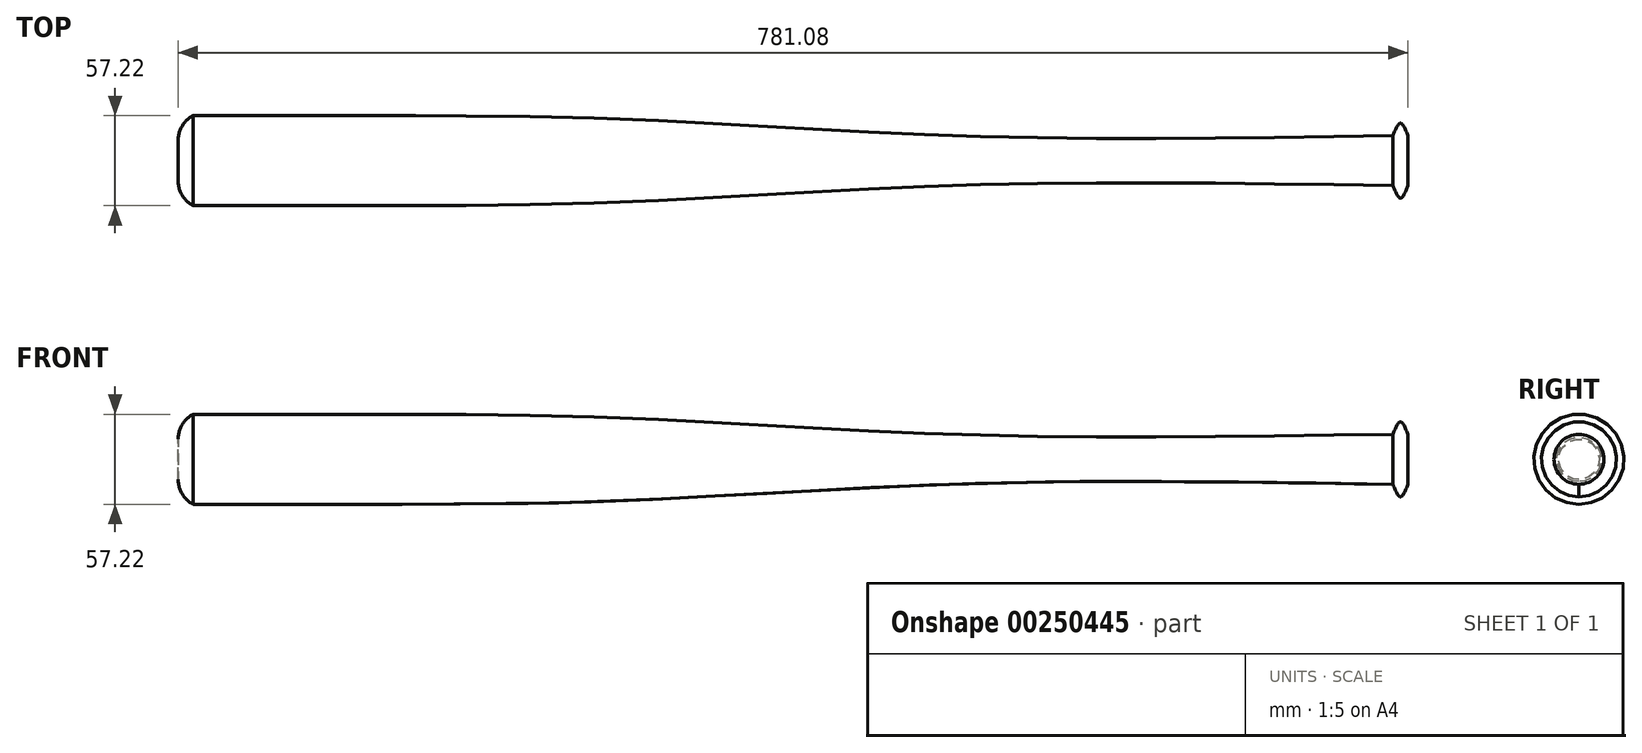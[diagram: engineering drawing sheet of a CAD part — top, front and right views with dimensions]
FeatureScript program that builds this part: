
annotation { "Feature Type Name" : "Feature", "Feature Type Description" : "" }
export const myFeature = defineFeature(function(context is Context, id is Id, definition is map)
    precondition{}
    {
        {
            var Q0;
            Q0=qCreatedBy(makeId("Right.planeOp"),FACE);
            var sketch = newSketch(context, id + "F0", { "sketchPlane" : qUnion([Q0])});
            skCircle(sketch, "E0", {"center": v(0, 0) * mm, "radius": 23.81 * mm});
            skSolve(sketch);
        }
        {
            var Q0;
            Q0=qCreatedBy(makeId("Right.planeOp"),FACE);
            cPlane(context, id + "F1", {"entities" : qUnion([Q0]), "cplaneType" : CPlaneType.OFFSET, "offset" : 4.78 * mm, "oppositeDirection" : true, "width" : 152.4 * mm, "height" : 152.4 * mm});
        }
        {
            var Q0;
            Q0=qCreatedBy(id+"F1.planeOp",FACE);
            var sketch = newSketch(context, id + "F2", { "sketchPlane" : qUnion([Q0])});
            skCircle(sketch, "E1", {"center": v(0, 0) * mm, "radius": 15.88 * mm});
            skSolve(sketch);
        }
        {
            var Q0;
            Q0=qCreatedBy(id+"F1.planeOp",FACE);
            cPlane(context, id + "F3", {"entities" : qUnion([Q0]), "cplaneType" : CPlaneType.OFFSET, "offset" : 127 * mm, "oppositeDirection" : true, "width" : 152.4 * mm, "height" : 152.4 * mm});
        }
        {
            var Q0;
            Q0=qCreatedBy(id+"F3.planeOp",FACE);
            var sketch = newSketch(context, id + "F4", { "sketchPlane" : qUnion([Q0])});
            skCircle(sketch, "E2", {"center": v(0, 0) * mm, "radius": 14.29 * mm});
            skSolve(sketch);
        }
        {
            var Q0;
            Q0=qCreatedBy(makeId("Right.planeOp"),FACE);
            cPlane(context, id + "F5", {"entities" : qUnion([Q0]), "cplaneType" : CPlaneType.OFFSET, "offset" : 4.78 * mm, "width" : 152.4 * mm, "height" : 152.4 * mm});
        }
        {
            var Q0;
            Q0=qCreatedBy(id+"F5.planeOp",FACE);
            var sketch = newSketch(context, id + "F6", { "sketchPlane" : qUnion([Q0])});
            skCircle(sketch, "E3", {"center": v(0, 0) * mm, "radius": 15.88 * mm});
            skSolve(sketch);
        }
        {
            var Q0;
            Q0=qCreatedBy(id+"F3.planeOp",FACE);
            cPlane(context, id + "F7", {"entities" : qUnion([Q0]), "cplaneType" : CPlaneType.OFFSET, "offset" : 127 * mm, "oppositeDirection" : true, "width" : 152.4 * mm, "height" : 152.4 * mm});
        }
        {
            var Q0;
            Q0=qCreatedBy(id+"F7.planeOp",FACE);
            var sketch = newSketch(context, id + "F8", { "sketchPlane" : qUnion([Q0])});
            skCircle(sketch, "E4", {"center": v(0, 0) * mm, "radius": 15.08 * mm});
            skSolve(sketch);
        }
        {
            var Q0;
            Q0=qCreatedBy(id+"F7.planeOp",FACE);
            cPlane(context, id + "F9", {"entities" : qUnion([Q0]), "cplaneType" : CPlaneType.OFFSET, "offset" : 127 * mm, "oppositeDirection" : true, "width" : 152.4 * mm, "height" : 152.4 * mm});
        }
        {
            var Q0;
            Q0=qCreatedBy(id+"F9.planeOp",FACE);
            var sketch = newSketch(context, id + "F10", { "sketchPlane" : qUnion([Q0])});
            skCircle(sketch, "E5", {"center": v(0, 0) * mm, "radius": 20.64 * mm});
            skSolve(sketch);
        }
        {
            var Q0;
            Q0=qCreatedBy(id+"F9.planeOp",FACE);
            cPlane(context, id + "F11", {"entities" : qUnion([Q0]), "cplaneType" : CPlaneType.OFFSET, "offset" : 127 * mm, "oppositeDirection" : true, "width" : 152.4 * mm, "height" : 152.4 * mm});
        }
        {
            var Q0;
            Q0=qCreatedBy(id+"F11.planeOp",FACE);
            var sketch = newSketch(context, id + "F12", { "sketchPlane" : qUnion([Q0])});
            skCircle(sketch, "E6", {"center": v(0, 0) * mm, "radius": 26.99 * mm});
            skSolve(sketch);
        }
        {
            var Q0;
            Q0=qCreatedBy(id+"F11.planeOp",FACE);
            cPlane(context, id + "F13", {"entities" : qUnion([Q0]), "cplaneType" : CPlaneType.OFFSET, "offset" : 127 * mm, "oppositeDirection" : true, "width" : 152.4 * mm, "height" : 152.4 * mm});
        }
        {
            var Q0;
            Q0=qCreatedBy(id+"F13.planeOp",FACE);
            var sketch = newSketch(context, id + "F14", { "sketchPlane" : qUnion([Q0])});
            skCircle(sketch, "E7", {"center": v(0, 0) * mm, "radius": 28.58 * mm});
            skSolve(sketch);
        }
        {
            var Q0;
            Q0=qCreatedBy(id+"F13.planeOp",FACE);
            cPlane(context, id + "F15", {"entities" : qUnion([Q0]), "cplaneType" : CPlaneType.OFFSET, "offset" : 127 * mm, "oppositeDirection" : true, "width" : 152.4 * mm, "height" : 152.4 * mm});
        }
        {
            var Q0;
            Q0=qCreatedBy(id+"F15.planeOp",FACE);
            var sketch = newSketch(context, id + "F16", { "sketchPlane" : qUnion([Q0])});
            skCircle(sketch, "E8", {"center": v(0, 0) * mm, "radius": 28.58 * mm});
            skSolve(sketch);
        }
        {
            var Q0;
            Q0=qCreatedBy(id+"F15.planeOp",FACE);
            cPlane(context, id + "F17", {"entities" : qUnion([Q0]), "cplaneType" : CPlaneType.OFFSET, "offset" : 9.52 * mm, "oppositeDirection" : true, "width" : 152.4 * mm, "height" : 152.4 * mm});
        }
        {
            var Q0;
            Q0=qCreatedBy(id+"F17.planeOp",FACE);
            var sketch = newSketch(context, id + "F18", { "sketchPlane" : qUnion([Q0])});
            skCircle(sketch, "E9", {"center": v(0, 0) * mm, "radius": 23.81 * mm});
            skSolve(sketch);
        }
        {
            var Q0;
            Q0=makeQuery(id+"F6.imprint","IMPRINT",FACE,{"disambiguationData":[TD([[makeQuery(id+"F6.imprint","IMPRINT",EDGE,{"derivedFrom":sQuery(id+"F6.wireOp",EDGE,"E3")}),1.0]])]});
            var Q1;
            Q1=makeQuery(id+"F0.imprint","IMPRINT",FACE,{"disambiguationData":[TD([[makeQuery(id+"F0.imprint","IMPRINT",EDGE,{"derivedFrom":sQuery(id+"F0.wireOp",EDGE,"E0")}),1.0]])]});
            var Q2;
            Q2=makeQuery(id+"F2.imprint","IMPRINT",FACE,{"disambiguationData":[TD([[makeQuery(id+"F2.imprint","IMPRINT",EDGE,{"derivedFrom":sQuery(id+"F2.wireOp",EDGE,"E1")}),1.0]])]});
            loft(context, id + "F19", {"sheetProfilesArray" : [{ "sheetProfileEntities" : qUnion([Q0]) }, { "sheetProfileEntities" : qUnion([Q1]) }, { "sheetProfileEntities" : qUnion([Q2]) }]});
        }
        {
            var Q1;
            Q1=makeQuery(id+"F19.opLoft","CAP_FACE",FACE,{"disambiguationData":[OSD([makeQuery(id+"F2.imprint","IMPRINT",FACE,{"disambiguationData":[TD([[makeQuery(id+"F2.imprint","IMPRINT",EDGE,{"derivedFrom":sQuery(id+"F2.wireOp",EDGE,"E1")}),1.0]])]})])],"isStart":true});
            var Q2;
            Q2=makeQuery(id+"F4.imprint","IMPRINT",FACE,{"disambiguationData":[TD([[makeQuery(id+"F4.imprint","IMPRINT",EDGE,{"derivedFrom":sQuery(id+"F4.wireOp",EDGE,"E2")}),1.0]])]});
            var Q3;
            Q3=makeQuery(id+"F8.imprint","IMPRINT",FACE,{"disambiguationData":[TD([[makeQuery(id+"F8.imprint","IMPRINT",EDGE,{"derivedFrom":sQuery(id+"F8.wireOp",EDGE,"E4")}),1.0]])]});
            var Q4;
            Q4=makeQuery(id+"F10.imprint","IMPRINT",FACE,{"disambiguationData":[TD([[makeQuery(id+"F10.imprint","IMPRINT",EDGE,{"derivedFrom":sQuery(id+"F10.wireOp",EDGE,"E5")}),1.0]])]});
            var Q5;
            Q5=makeQuery(id+"F12.imprint","IMPRINT",FACE,{"disambiguationData":[TD([[makeQuery(id+"F12.imprint","IMPRINT",EDGE,{"derivedFrom":sQuery(id+"F12.wireOp",EDGE,"E6")}),1.0]])]});
            var Q6;
            Q6=makeQuery(id+"F14.imprint","IMPRINT",FACE,{"disambiguationData":[TD([[makeQuery(id+"F14.imprint","IMPRINT",EDGE,{"derivedFrom":sQuery(id+"F14.wireOp",EDGE,"E7")}),1.0]])]});
            var Q7;
            Q7=makeQuery(id+"F16.imprint","IMPRINT",FACE,{"disambiguationData":[TD([[makeQuery(id+"F16.imprint","IMPRINT",EDGE,{"derivedFrom":sQuery(id+"F16.wireOp",EDGE,"E8")}),1.0]])]});
            loft(context, id + "F20", {"operationType" : NewBodyOperationType.ADD, "sheetProfilesArray" : [{ "sheetProfileEntities" : qUnion([Q1]) }, { "sheetProfileEntities" : qUnion([Q2]) }, { "sheetProfileEntities" : qUnion([Q3]) }, { "sheetProfileEntities" : qUnion([Q4]) }, { "sheetProfileEntities" : qUnion([Q5]) }, { "sheetProfileEntities" : qUnion([Q6]) }, { "sheetProfileEntities" : qUnion([Q7]) }]});
        }
        {
            var Q1;
            Q1=makeQuery(id+"F20.opLoft","CAP_FACE",FACE,{"disambiguationData":[OSD([makeQuery(id+"F16.imprint","IMPRINT",FACE,{"disambiguationData":[TD([[makeQuery(id+"F16.imprint","IMPRINT",EDGE,{"derivedFrom":sQuery(id+"F16.wireOp",EDGE,"E8")}),1.0]])]})])],"isStart":true});
            var Q2;
            Q2=makeQuery(id+"F18.imprint","IMPRINT",FACE,{"disambiguationData":[TD([[makeQuery(id+"F18.imprint","IMPRINT",EDGE,{"derivedFrom":sQuery(id+"F18.wireOp",EDGE,"E9")}),1.0]])]});
            loft(context, id + "F21", {"operationType" : NewBodyOperationType.ADD, "sheetProfilesArray" : [{ "sheetProfileEntities" : qUnion([Q1]) }, { "sheetProfileEntities" : qUnion([Q2]) }]});
        }
        {
            var Q0;
            Q0=makeQuery(id+"F21.opLoft","MID_CAP_EDGE",EDGE,{"disambiguationData":[OSD([sQuery(id+"F2.wireOp",EDGE,"E1"),sQuery(id+"F6.wireOp",EDGE,"E3"),sQuery(id+"F16.wireOp",EDGE,"E8"),sQuery(id+"F18.wireOp",EDGE,"E9")])],"capPos":1.0});
            fillet(context, id + "F22", {"entities" : qUnion([Q0]), "radius" : 17.78 * mm, "tangentPropagation" : true, "allowEdgeOverflow" : false});
        }
    });
